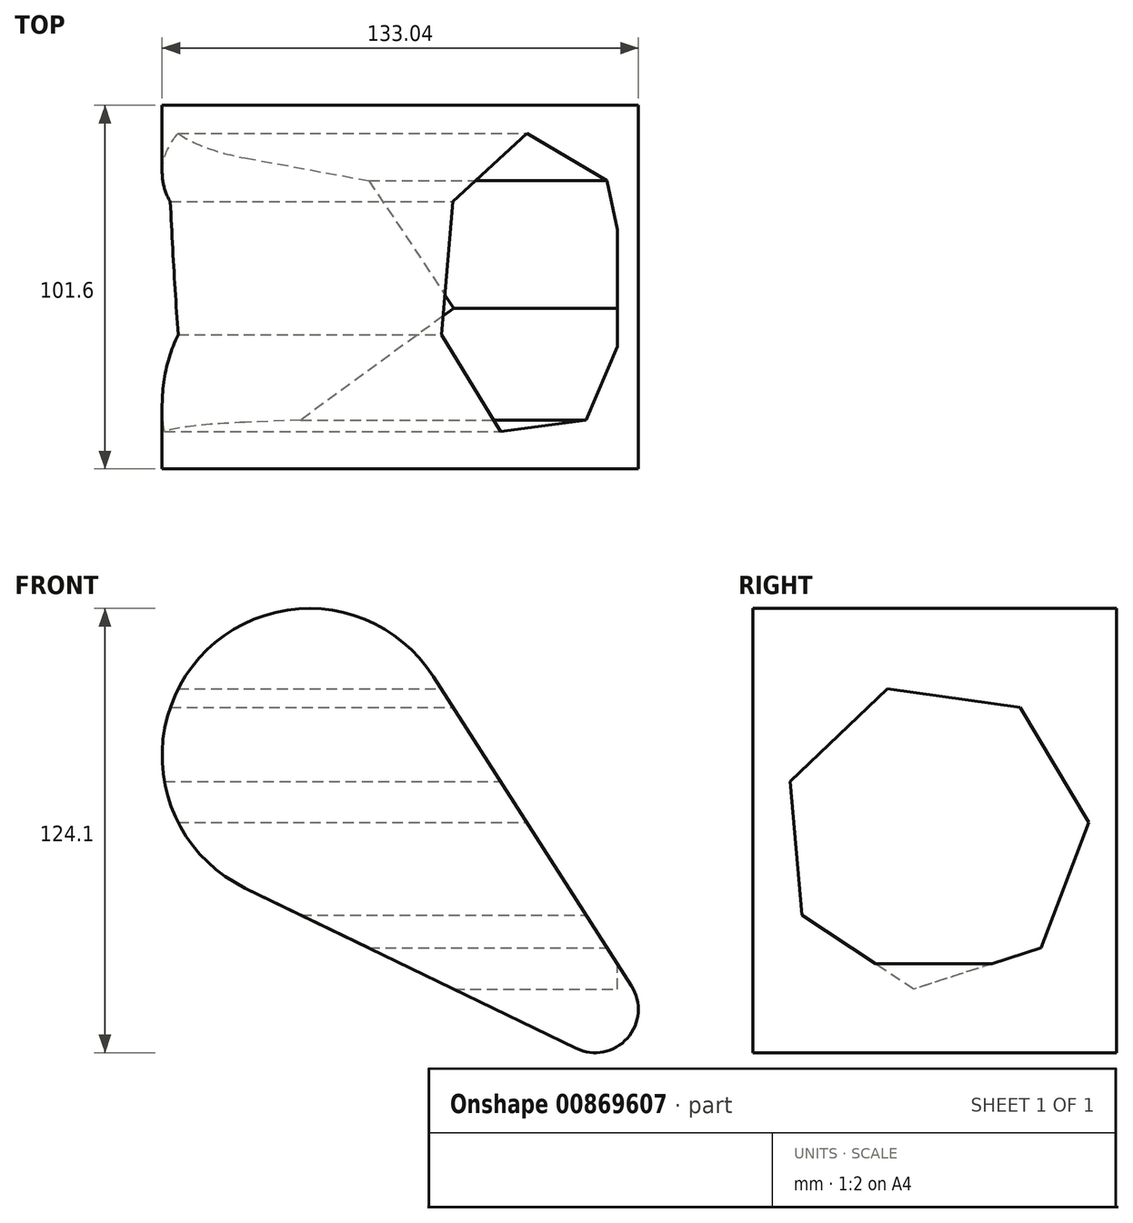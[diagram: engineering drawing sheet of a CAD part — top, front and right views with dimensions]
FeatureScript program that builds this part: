
annotation { "Feature Type Name" : "Feature", "Feature Type Description" : "" }
export const myFeature = defineFeature(function(context is Context, id is Id, definition is map)
    precondition{}
    {
        {
            var Q0;
            Q0=qCreatedBy(makeId("Front.planeOp"),FACE);
            var sketch = newSketch(context, id + "F0", { "sketchPlane" : qUnion([Q0])});
            skCircle(sketch, "E0", {"center": v(-49.2, 48.32) * mm, "radius": 41.12 * mm});
            skCircle(sketch, "E1", {"center": v(30.64, -22.59) * mm, "radius": 12.08 * mm});
            skLineSegment(sketch, "E2", {"start": v(-14.57, 70.48) * mm, "end": v(40.82, -16.08) * mm});
            skLineSegment(sketch, "E3", {"start": v(-67.11, 11.31) * mm, "end": v(25.38, -33.47) * mm});
            skSolve(sketch);
        }
        {
            var Q0;
            Q0 = qSketchRegion(id + "F0", true);
            extrude(context, id + "F1", {"entities" : qUnion([Q0]), "endBound" : BoundingType.SYMMETRIC, "depth" : 101.6 * mm, "offsetDistance" : 25.4 * mm});
        }
        {
            var Q0;
            Q0=qCreatedBy(makeId("Right.planeOp"),FACE);
            var sketch = newSketch(context, id + "F2", { "sketchPlane" : qUnion([Q0])});
            skCircle(sketch, "E4.cCircle", {"center": v(0, 25.85) * mm, "radius": 38.9 * mm, "construction": true});
            skLineSegment(sketch, "E4.0", {"start": v(-40.38, 41.12) * mm, "end": v(-13.24, 66.95) * mm});
            skLineSegment(sketch, "E4.1", {"start": v(-13.24, 66.95) * mm, "end": v(23.87, 61.83) * mm});
            skLineSegment(sketch, "E4.2", {"start": v(23.87, 61.83) * mm, "end": v(43, 29.62) * mm});
            skLineSegment(sketch, "E4.3", {"start": v(43, 29.62) * mm, "end": v(29.76, -5.42) * mm});
            skLineSegment(sketch, "E4.4", {"start": v(29.76, -5.42) * mm, "end": v(-5.9, -16.91) * mm});
            skLineSegment(sketch, "E4.5", {"start": v(-5.9, -16.91) * mm, "end": v(-37.11, 3.8) * mm});
            skLineSegment(sketch, "E4.6", {"start": v(-37.11, 3.8) * mm, "end": v(-40.38, 41.12) * mm});
            skPoint(sketch, "E4.0.midPoint", {"position": v(-26.81, 54.03) * mm});
            skSolve(sketch);
        }
        {
            var Q0;
            Q0 = qSketchRegion(id + "F2", true);
            extrude(context, id + "F3", {"entities" : qUnion([Q0]), "operationType" : NewBodyOperationType.REMOVE, "oppositeDirection" : true, "depth" : 111 * mm, "offsetDistance" : 25.4 * mm, "hasSecondDirection" : true, "secondDirectionOppositeDirection" : false, "secondDirectionDepth" : 36.83 * mm});
        }
    });
